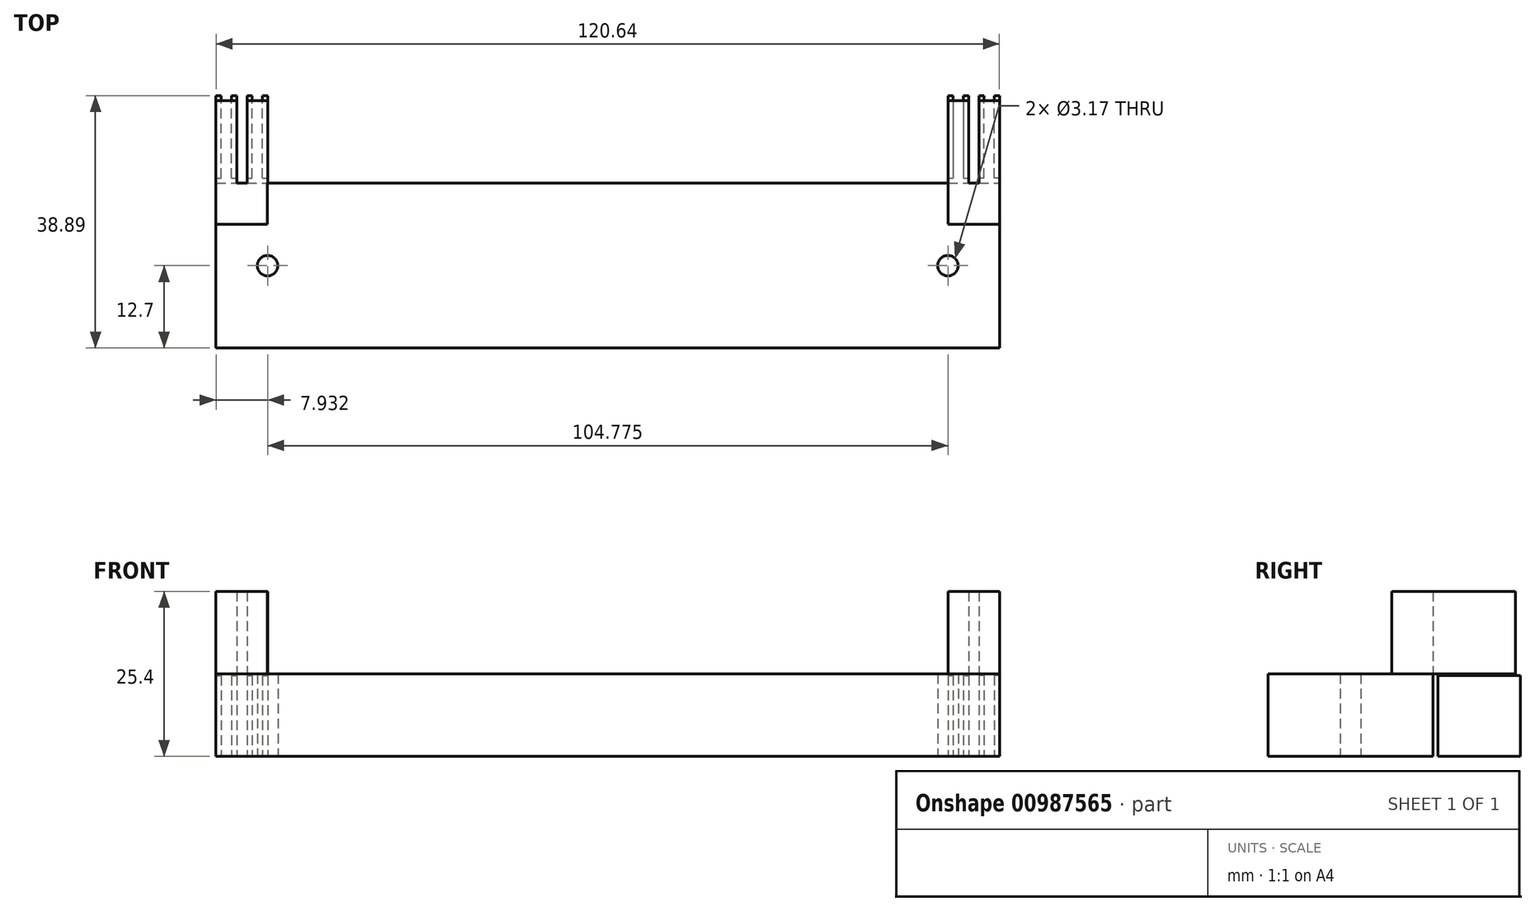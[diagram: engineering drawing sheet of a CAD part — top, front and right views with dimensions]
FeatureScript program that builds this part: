
annotation { "Feature Type Name" : "Feature", "Feature Type Description" : "" }
export const myFeature = defineFeature(function(context is Context, id is Id, definition is map)
    precondition{}
    {
        {
            var Q0;
            Q0=qCreatedBy(makeId("Top.planeOp"),FACE);
            var sketch = newSketch(context, id + "F0", { "sketchPlane" : qUnion([Q0])});
            skLineSegment(sketch, "E0.bottom", {"start": v(-60.33, 12.7) * mm, "end": v(60.33, 12.7) * mm});
            skLineSegment(sketch, "E0.top", {"start": v(-60.33, -12.7) * mm, "end": v(60.33, -12.7) * mm});
            skLineSegment(sketch, "E0.left", {"start": v(-60.32, 12.7) * mm, "end": v(-60.33, -12.7) * mm});
            skLineSegment(sketch, "E0.right", {"start": v(60.33, 12.7) * mm, "end": v(60.33, -12.7) * mm});
            skPoint(sketch, "E0.middle", {"position": v(0, 0) * mm});
            skLineSegment(sketch, "E1.bottom", {"start": v(-60.33, 13.5) * mm, "end": v(-59.53, 13.5) * mm});
            skLineSegment(sketch, "E1.top", {"start": v(-60.33, 26.2) * mm, "end": v(-59.53, 26.2) * mm});
            skLineSegment(sketch, "E1.left", {"start": v(-60.33, 13.5) * mm, "end": v(-60.33, 26.2) * mm});
            skLineSegment(sketch, "E1.right", {"start": v(-59.53, 13.5) * mm, "end": v(-59.53, 26.2) * mm});
            skLineSegment(sketch, "E2.bottom", {"start": v(-57.94, 13.5) * mm, "end": v(-57.15, 13.5) * mm});
            skLineSegment(sketch, "E2.top", {"start": v(-57.94, 26.2) * mm, "end": v(-57.15, 26.2) * mm});
            skLineSegment(sketch, "E2.left", {"start": v(-57.94, 13.5) * mm, "end": v(-57.94, 26.2) * mm});
            skLineSegment(sketch, "E2.right", {"start": v(-57.15, 13.5) * mm, "end": v(-57.15, 26.2) * mm});
            skLineSegment(sketch, "E3.bottom", {"start": v(60.33, 13.5) * mm, "end": v(59.53, 13.5) * mm});
            skLineSegment(sketch, "E3.top", {"start": v(60.32, 26.2) * mm, "end": v(59.53, 26.2) * mm});
            skLineSegment(sketch, "E3.left", {"start": v(60.33, 13.5) * mm, "end": v(60.33, 26.2) * mm});
            skLineSegment(sketch, "E3.right", {"start": v(59.53, 13.5) * mm, "end": v(59.53, 26.2) * mm});
            skLineSegment(sketch, "E4.bottom", {"start": v(57.94, 13.5) * mm, "end": v(57.15, 13.5) * mm});
            skLineSegment(sketch, "E4.top", {"start": v(57.94, 26.2) * mm, "end": v(57.15, 26.2) * mm});
            skLineSegment(sketch, "E4.left", {"start": v(57.94, 13.5) * mm, "end": v(57.94, 26.2) * mm});
            skLineSegment(sketch, "E4.right", {"start": v(57.15, 13.5) * mm, "end": v(57.15, 26.2) * mm});
            skLineSegment(sketch, "E5.bottom", {"start": v(-55.56, 13.5) * mm, "end": v(-54.77, 13.5) * mm});
            skLineSegment(sketch, "E5.top", {"start": v(-55.56, 26.2) * mm, "end": v(-54.77, 26.2) * mm});
            skLineSegment(sketch, "E5.left", {"start": v(-55.56, 13.5) * mm, "end": v(-55.56, 26.2) * mm});
            skLineSegment(sketch, "E5.right", {"start": v(-54.77, 13.5) * mm, "end": v(-54.77, 26.2) * mm});
            skLineSegment(sketch, "E6.bottom", {"start": v(-53.18, 13.5) * mm, "end": v(-52.39, 13.5) * mm});
            skLineSegment(sketch, "E6.top", {"start": v(-53.18, 26.2) * mm, "end": v(-52.39, 26.2) * mm});
            skLineSegment(sketch, "E6.left", {"start": v(-53.18, 13.5) * mm, "end": v(-53.18, 26.2) * mm});
            skLineSegment(sketch, "E6.right", {"start": v(-52.39, 13.5) * mm, "end": v(-52.39, 26.2) * mm});
            skLineSegment(sketch, "E7.bottom", {"start": v(54.77, 26.2) * mm, "end": v(55.56, 26.2) * mm});
            skLineSegment(sketch, "E7.top", {"start": v(54.77, 13.5) * mm, "end": v(55.56, 13.5) * mm});
            skLineSegment(sketch, "E7.left", {"start": v(54.77, 26.2) * mm, "end": v(54.77, 13.5) * mm});
            skLineSegment(sketch, "E7.right", {"start": v(55.56, 26.2) * mm, "end": v(55.56, 13.5) * mm});
            skLineSegment(sketch, "E8.bottom", {"start": v(52.39, 26.2) * mm, "end": v(53.18, 26.2) * mm});
            skLineSegment(sketch, "E8.top", {"start": v(52.39, 13.5) * mm, "end": v(53.18, 13.5) * mm});
            skLineSegment(sketch, "E8.left", {"start": v(52.39, 26.2) * mm, "end": v(52.39, 13.5) * mm});
            skLineSegment(sketch, "E8.right", {"start": v(53.18, 26.2) * mm, "end": v(53.18, 13.5) * mm});
            skCircle(sketch, "E9", {"center": v(-52.39, 0) * mm, "radius": 1.59 * mm});
            skCircle(sketch, "E10", {"center": v(52.39, 0) * mm, "radius": 1.59 * mm});
            skSolve(sketch);
        }
        {
            var Q0;
            Q0=makeQuery(id+"F0.imprint","IMPRINT",FACE,{"disambiguationData":[TD([[makeQuery(id+"F0.imprint","IMPRINT",EDGE,{"derivedFrom":sQuery(id+"F0.wireOp",EDGE,"E0.bottom")}),-1.0]])]});
            extrude(context, id + "F1", {"entities" : qUnion([Q0]), "depth" : 12.7 * mm, "offsetDistance" : 25.4 * mm});
        }
        {
            var Q0;
            Q0=makeQuery(id+"F0.imprint","IMPRINT",FACE,{"disambiguationData":[TD([[makeQuery(id+"F0.imprint","IMPRINT",EDGE,{"derivedFrom":sQuery(id+"F0.wireOp",EDGE,"E1.bottom")}),1.0]])]});
            var Q1;
            Q1=makeQuery(id+"F0.imprint","IMPRINT",FACE,{"disambiguationData":[TD([[makeQuery(id+"F0.imprint","IMPRINT",EDGE,{"derivedFrom":sQuery(id+"F0.wireOp",EDGE,"E2.bottom")}),1.0]])]});
            var Q2;
            Q2=makeQuery(id+"F0.imprint","IMPRINT",FACE,{"disambiguationData":[TD([[makeQuery(id+"F0.imprint","IMPRINT",EDGE,{"derivedFrom":sQuery(id+"F0.wireOp",EDGE,"E5.bottom")}),1.0]])]});
            var Q3;
            Q3=makeQuery(id+"F0.imprint","IMPRINT",FACE,{"disambiguationData":[TD([[makeQuery(id+"F0.imprint","IMPRINT",EDGE,{"derivedFrom":sQuery(id+"F0.wireOp",EDGE,"E6.bottom")}),1.0]])]});
            var Q4;
            Q4=makeQuery(id+"F0.imprint","IMPRINT",FACE,{"disambiguationData":[TD([[makeQuery(id+"F0.imprint","IMPRINT",EDGE,{"derivedFrom":sQuery(id+"F0.wireOp",EDGE,"E8.bottom")}),-1.0]])]});
            var Q5;
            Q5=makeQuery(id+"F0.imprint","IMPRINT",FACE,{"disambiguationData":[TD([[makeQuery(id+"F0.imprint","IMPRINT",EDGE,{"derivedFrom":sQuery(id+"F0.wireOp",EDGE,"E7.bottom")}),-1.0]])]});
            var Q6;
            Q6=makeQuery(id+"F0.imprint","IMPRINT",FACE,{"disambiguationData":[TD([[makeQuery(id+"F0.imprint","IMPRINT",EDGE,{"derivedFrom":sQuery(id+"F0.wireOp",EDGE,"E4.bottom")}),-1.0]])]});
            var Q7;
            Q7=makeQuery(id+"F0.imprint","IMPRINT",FACE,{"disambiguationData":[TD([[makeQuery(id+"F0.imprint","IMPRINT",EDGE,{"derivedFrom":sQuery(id+"F0.wireOp",EDGE,"E3.bottom")}),-1.0]])]});
            extrude(context, id + "F2", {"entities" : qUnion([Q0, Q1, Q2, Q3, Q4, Q5, Q6, Q7]), "depth" : 12.45 * mm, "offsetDistance" : 25.4 * mm});
        }
        {
            var Q0;
            Q0=makeQuery(id+"F1.opExtrude","CAP_FACE",FACE,{"disambiguationData":[OSD([sQuery(id+"F0.wireOp",EDGE,"E0.bottom"),sQuery(id+"F0.wireOp",EDGE,"E0.top"),sQuery(id+"F0.wireOp",EDGE,"E0.left"),sQuery(id+"F0.wireOp",EDGE,"E0.right"),sQuery(id+"F0.wireOp",EDGE,"E9"),sQuery(id+"F0.wireOp",EDGE,"E10")])],"isStart":false});
            var sketch = newSketch(context, id + "F3", { "sketchPlane" : qUnion([Q0])});
            skLineSegment(sketch, "E11.bottom", {"start": v(-60.33, 12.7) * mm, "end": v(-57.15, 12.7) * mm});
            skLineSegment(sketch, "E11.top", {"start": v(-60.33, 25.4) * mm, "end": v(-57.15, 25.4) * mm});
            skLineSegment(sketch, "E11.left", {"start": v(-60.33, 12.7) * mm, "end": v(-60.33, 25.4) * mm});
            skLineSegment(sketch, "E11.right", {"start": v(-57.15, 12.7) * mm, "end": v(-57.15, 25.4) * mm});
            skLineSegment(sketch, "E12.bottom", {"start": v(-55.56, 12.7) * mm, "end": v(-52.39, 12.7) * mm});
            skLineSegment(sketch, "E12.top", {"start": v(-55.56, 25.4) * mm, "end": v(-52.39, 25.4) * mm});
            skLineSegment(sketch, "E12.left", {"start": v(-55.56, 12.7) * mm, "end": v(-55.56, 25.4) * mm});
            skLineSegment(sketch, "E12.right", {"start": v(-52.39, 12.7) * mm, "end": v(-52.39, 25.4) * mm});
            skLineSegment(sketch, "E13.bottom", {"start": v(60.33, 12.7) * mm, "end": v(57.15, 12.7) * mm});
            skLineSegment(sketch, "E13.top", {"start": v(60.32, 25.4) * mm, "end": v(57.15, 25.4) * mm});
            skLineSegment(sketch, "E13.left", {"start": v(60.33, 12.7) * mm, "end": v(60.33, 25.4) * mm});
            skLineSegment(sketch, "E13.right", {"start": v(57.15, 12.7) * mm, "end": v(57.15, 25.4) * mm});
            skLineSegment(sketch, "E14.bottom", {"start": v(52.39, 12.7) * mm, "end": v(55.56, 12.7) * mm});
            skLineSegment(sketch, "E14.top", {"start": v(52.39, 25.4) * mm, "end": v(55.56, 25.4) * mm});
            skLineSegment(sketch, "E14.left", {"start": v(52.39, 12.7) * mm, "end": v(52.39, 25.4) * mm});
            skLineSegment(sketch, "E14.right", {"start": v(55.56, 12.7) * mm, "end": v(55.56, 25.4) * mm});
            skLineSegment(sketch, "E15.bottom", {"start": v(-60.33, 12.7) * mm, "end": v(-52.4, 12.7) * mm});
            skLineSegment(sketch, "E15.top", {"start": v(-60.33, 6.35) * mm, "end": v(-52.4, 6.35) * mm});
            skLineSegment(sketch, "E15.left", {"start": v(-60.33, 12.7) * mm, "end": v(-60.33, 6.35) * mm});
            skLineSegment(sketch, "E15.right", {"start": v(-52.4, 12.7) * mm, "end": v(-52.4, 6.35) * mm});
            skLineSegment(sketch, "E16.bottom", {"start": v(60.33, 12.7) * mm, "end": v(52.41, 12.7) * mm});
            skLineSegment(sketch, "E16.top", {"start": v(60.33, 6.35) * mm, "end": v(52.41, 6.35) * mm});
            skLineSegment(sketch, "E16.left", {"start": v(60.33, 12.7) * mm, "end": v(60.33, 6.35) * mm});
            skLineSegment(sketch, "E16.right", {"start": v(52.41, 12.7) * mm, "end": v(52.41, 6.35) * mm});
            skSolve(sketch);
        }
        {
            var Q0;
            Q0=makeQuery(id+"F3.imprint","IMPRINT",FACE,{"disambiguationData":[TD([[makeQuery(id+"F3.imprint","IMPRINT",EDGE,{"derivedFrom":sQuery(id+"F3.wireOp",EDGE,"E11.top")}),-1.0]])]});
            var Q1;
            {var subQ2=sQuery(id+"F3.wireOp",EDGE,"E12.bottom");Q1=makeQuery(id+"F3.imprint","IMPRINT",FACE,{"disambiguationData":[TD([[makeQuery(id+"F3.imprint","IMPRINT",EDGE,{"derivedFrom":subQ2}),1.0]])]});}
            var Q2;
            {var subQ1=sQuery(id+"F3.wireOp",EDGE,"E14.bottom");Q2=makeQuery(id+"F3.imprint","IMPRINT",FACE,{"disambiguationData":[TD([[makeQuery(id+"F3.imprint","IMPRINT",EDGE,{"derivedFrom":subQ1}),1.0]])]});}
            var Q3;
            Q3=makeQuery(id+"F3.imprint","IMPRINT",FACE,{"disambiguationData":[TD([[makeQuery(id+"F3.imprint","IMPRINT",EDGE,{"derivedFrom":sQuery(id+"F3.wireOp",EDGE,"E13.top")}),1.0]])]});
            var Q4;
            Q4=makeQuery(id+"F3.imprint","IMPRINT",FACE,{"disambiguationData":[TD([[makeQuery(id+"F3.imprint","IMPRINT",EDGE,{"derivedFrom":sQuery(id+"F3.wireOp",EDGE,"E15.top")}),1.0]])]});
            var Q5;
            Q5=makeQuery(id+"F3.imprint","IMPRINT",FACE,{"disambiguationData":[TD([[makeQuery(id+"F3.imprint","IMPRINT",EDGE,{"derivedFrom":sQuery(id+"F3.wireOp",EDGE,"E16.top")}),-1.0]])]});
            extrude(context, id + "F4", {"entities" : qUnion([Q0, Q1, Q2, Q3, Q4, Q5]), "depth" : 12.7 * mm, "offsetDistance" : 25.4 * mm});
        }
    });
